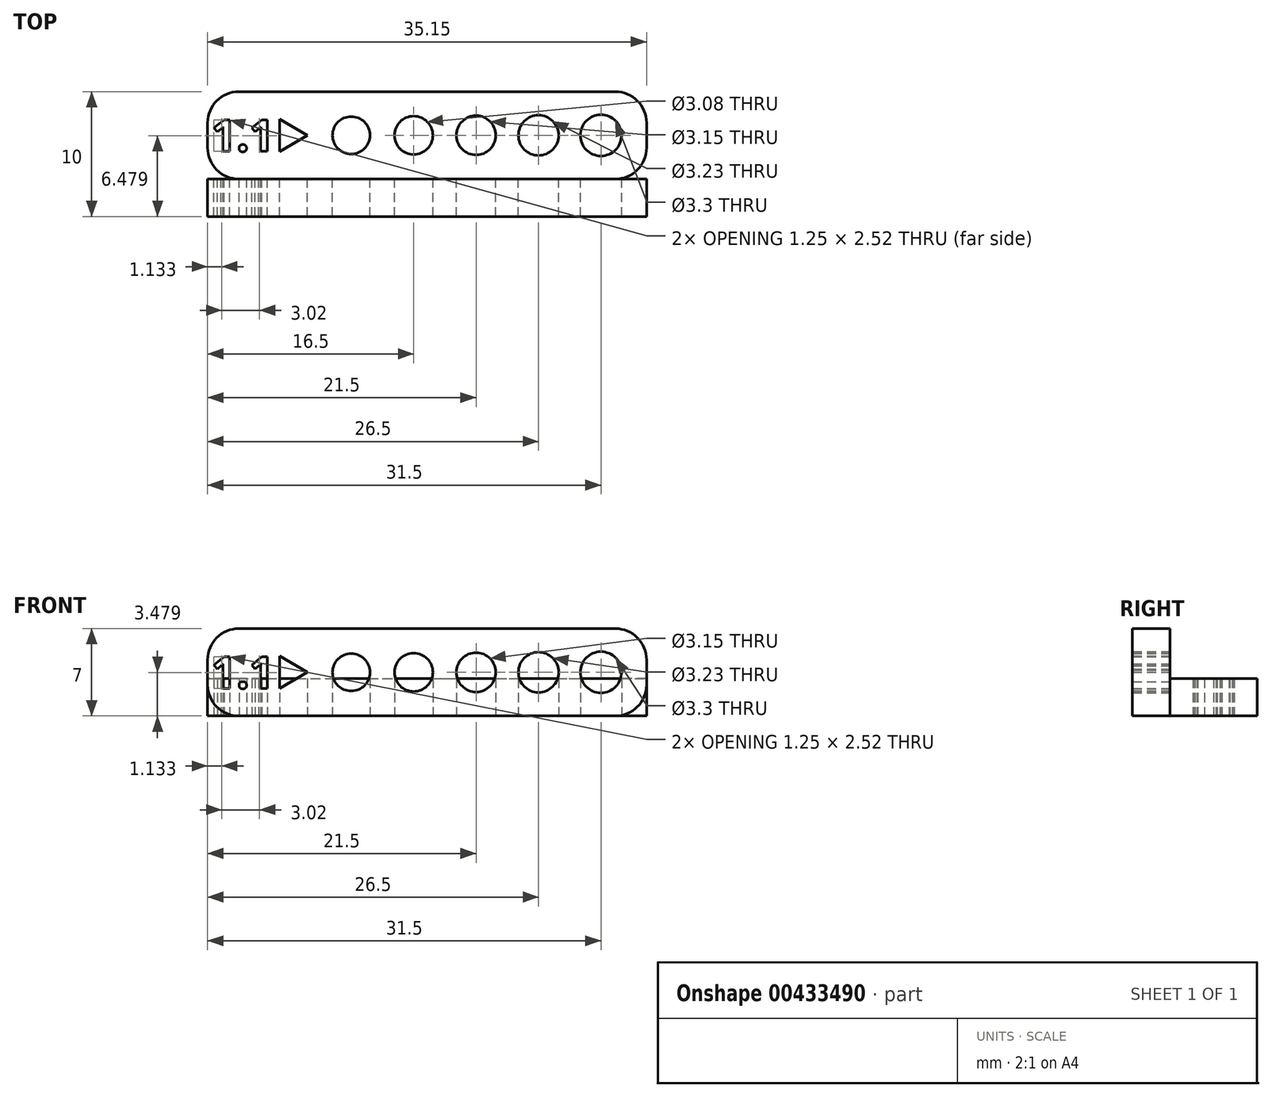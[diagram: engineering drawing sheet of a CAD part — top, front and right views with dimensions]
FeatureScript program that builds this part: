
annotation { "Feature Type Name" : "Feature", "Feature Type Description" : "" }
export const myFeature = defineFeature(function(context is Context, id is Id, definition is map)
    precondition{}
    {
        {
            var Q0;
            Q0=qCreatedBy(makeId("Top.planeOp"),FACE);
            var sketch = newSketch(context, id + "F0", { "sketchPlane" : qUnion([Q0])});
            skCircle(sketch, "E0", {"center": v(0, 0) * mm, "radius": 1.5 * mm});
            skCircle(sketch, "E1.1.0.0", {"center": v(5, 0) * mm, "radius": 1.54 * mm});
            skCircle(sketch, "E1.2.0.0", {"center": v(10, 0) * mm, "radius": 1.57 * mm});
            skCircle(sketch, "E1.3.0.0", {"center": v(15, 0) * mm, "radius": 1.61 * mm});
            skCircle(sketch, "E1.4.0.0", {"center": v(20, 0) * mm, "radius": 1.65 * mm});
            skLineSegment(sketch, "E2", {"start": v(0, 0) * mm, "end": v(20, 0) * mm, "construction": true});
            skCircle(sketch, "E3.cCircle", {"center": v(-5, 0) * mm, "radius": 1.5 * mm, "construction": true});
            skLineSegment(sketch, "E3.0", {"start": v(-3.5, 0) * mm, "end": v(-5.75, -1.3) * mm});
            skLineSegment(sketch, "E3.1", {"start": v(-5.75, -1.3) * mm, "end": v(-5.75, 1.3) * mm});
            skLineSegment(sketch, "E3.2", {"start": v(-5.75, 1.3) * mm, "end": v(-3.5, 0) * mm});
            skLineSegment(sketch, "E4.bottom", {"start": v(-9, 3.5) * mm, "end": v(21.15, 3.5) * mm});
            skLineSegment(sketch, "E4.top", {"start": v(-9, -3.5) * mm, "end": v(21.15, -3.5) * mm});
            skLineSegment(sketch, "E4.left", {"start": v(-11.5, 1) * mm, "end": v(-11.5, -1) * mm});
            skLineSegment(sketch, "E4.right", {"start": v(23.65, 1) * mm, "end": v(23.65, -1) * mm});
            skPoint(sketch, "E5.visualSharp", {"position": v(-11.5, 3.5) * mm});
            skArc(sketch, "E5.filletArc", {"start": v(-9, 3.5) * mm, "mid": v(-10.77, 2.77) * mm, "end": v(-11.5, 1) * mm});
            skPoint(sketch, "E6.visualSharp", {"position": v(-11.5, -3.5) * mm});
            skArc(sketch, "E6.filletArc", {"start": v(-11.5, -1) * mm, "mid": v(-10.77, -2.77) * mm, "end": v(-9, -3.5) * mm});
            skPoint(sketch, "E7.visualSharp", {"position": v(23.65, 3.5) * mm});
            skArc(sketch, "E7.filletArc", {"start": v(23.65, 1) * mm, "mid": v(22.92, 2.77) * mm, "end": v(21.15, 3.5) * mm});
            skPoint(sketch, "E8.visualSharp", {"position": v(23.65, -3.5) * mm});
            skArc(sketch, "E8.filletArc", {"start": v(21.15, -3.5) * mm, "mid": v(22.92, -2.77) * mm, "end": v(23.65, -1) * mm});
            skText(sketch, "E9", { "text": "1.1", "fontName": "OpenSans-Bold.ttf"});
            const initialGuessF0  = {"E9": [-0.0112, -0.00128, 1, 0, 0.00254]};
            skSetInitialGuess(sketch, initialGuessF0);
            skSolve(sketch);
        }
        {
            var Q0;
            Q0=makeQuery(id+"F0.imprint","IMPRINT",FACE,{"disambiguationData":[TD([[makeQuery(id+"F0.imprint","IMPRINT",EDGE,{"derivedFrom":sQuery(id+"F0.wireOp",EDGE,"E0")}),-1.0]])]});
            extrude(context, id + "F1", {"entities" : qUnion([Q0]), "depth" : 3 * mm});
        }
        {
            var Q0;
            Q0=makeQuery(id+"F0.imprint","IMPRINT",FACE,{"disambiguationData":[TD([[makeQuery(id+"F0.imprint","IMPRINT",EDGE,{"derivedFrom":sQuery(id+"F0.wireOp",EDGE,"E0")}),-1.0]])]});
            extrude(context, id + "F2", {"entities" : qUnion([Q0]), "depth" : 3 * mm});
        }
        {
            var Q0;
            Q0=makeQuery(id+"F2.opExtrude","SWEPT_BODY",BODY,{"disambiguationData":[OSD([sQuery(id+"F0.wireOp",EDGE,"E0"),sQuery(id+"F0.wireOp",EDGE,"E1.1.0.0"),sQuery(id+"F0.wireOp",EDGE,"E1.2.0.0"),sQuery(id+"F0.wireOp",EDGE,"E1.3.0.0"),sQuery(id+"F0.wireOp",EDGE,"E1.4.0.0"),sQuery(id+"F0.wireOp",EDGE,"E3.0"),sQuery(id+"F0.wireOp",EDGE,"E3.1"),sQuery(id+"F0.wireOp",EDGE,"E3.2"),sQuery(id+"F0.wireOp",EDGE,"E4.bottom"),sQuery(id+"F0.wireOp",EDGE,"E4.top"),sQuery(id+"F0.wireOp",EDGE,"E4.left"),sQuery(id+"F0.wireOp",EDGE,"E4.right"),sQuery(id+"F0.wireOp",EDGE,"E5.filletArc"),sQuery(id+"F0.wireOp",EDGE,"E6.filletArc"),sQuery(id+"F0.wireOp",EDGE,"E7.filletArc"),sQuery(id+"F0.wireOp",EDGE,"E8.filletArc")])]});
            var Q1;
            Q1=makeQuery(id+"F2.opExtrude","CAP_EDGE",EDGE,{"disambiguationData":[OSD([sQuery(id+"F0.wireOp",EDGE,"E4.top")])],"isStart":true});
            transform(context, id + "F3", {"entities" : qUnion([Q0]), "transformType" : TransformType.ROTATION, "transformAxis" : qUnion([Q1]), "angle" : 90 * degree, "makeCopy" : false});
        }
    });
